# Revit family: SAE201
name_source: partatom
category: Lighting Fixtures
units: mm (PartAtom-declared; Revit-internal decimal feet)

## family parameters
Cut with Voids When Loaded = No
Host = Face
Light Source = No
OmniClass Number = 23.80.70.11.14.17
OmniClass Title = Direct/Indirect
Part Type = Normal
Room Calculation Point = No
Round Connector Dimension = Use Diameter
Shared = Yes

## types (4) — shared parameters
Angle option = MOD : 0 Degrees
Apparent Load = 0 VA
Assembly Code = D5020210
Backbox = Paint - Matte White
Default Elevation = 48 "
Description = SAE201 is a versatile, concealed, architectural cove light with the flexibility to adjust beam angle pre or post installation
Glass = White Glass
Lamp = Fluorescent
Light Distribution = Asymmetric Indirect
Load Classification = Lighting
Manufacturer = Litecontrol
Model = SAE201 Adjustable Concealed Cove
Mounting = Concealed Cove
Power Factor = 1
Type Comments = Lighting Fixture
URL = https://www.currentlighting.com
Voltage = 120 V
Warranty = 5 years warranty

## per-type parameters (varying)
| type | Angle Tilt | zz Angle 1 | zz Length 1 | zz Length 2 |
| SAE201-01 | 90.00° | 89.50° | 11.75 " | 12 " |
| SAE201-02 | 90.00° | 89.50° | 23.75 " | 24 " |
| SAE201-03 | 90.00° | 89.50° | 35.75 " | 36 " |
| SAE201-04 | 0.00° | 0.50° | 47.75 " | 48 " |

## geometry (parser evidence)
native form markers: Sweep x7
no freeform markers — native parametric forms only
